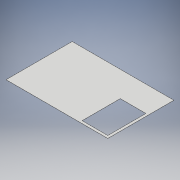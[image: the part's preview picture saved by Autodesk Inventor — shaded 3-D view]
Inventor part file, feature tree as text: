
AUTODESK INVENTOR PART (.ipt)
format: ipt  version: 2017 (Build 210142000, 142)  size: 109,568 bytes
history: native  units: mm
features: sketch x2, other x2, sheet_metal_op x1
ambient origin geometry x8: Origin, YZ Plane, XZ Plane, XY Plane, X Axis, Y Axis, Z Axis, Center Point
bodies: Solid1 (feature_tree)
feature tree (5):
  sheet_metal_op  "Face1"
  sketch  "Sketch1"  dims[d0=400.0mm]
  other  "Plate1"
  sketch  "Sketch2"  dims[d1=260.0mm d2=0.5mm d3=380.0mm d4=240.0mm d5=244.0mm d6=244.0mm d7=101.0mm d8=150.0mm d9=0.5mm d10=0.0mm]
  other  "Cut1"
